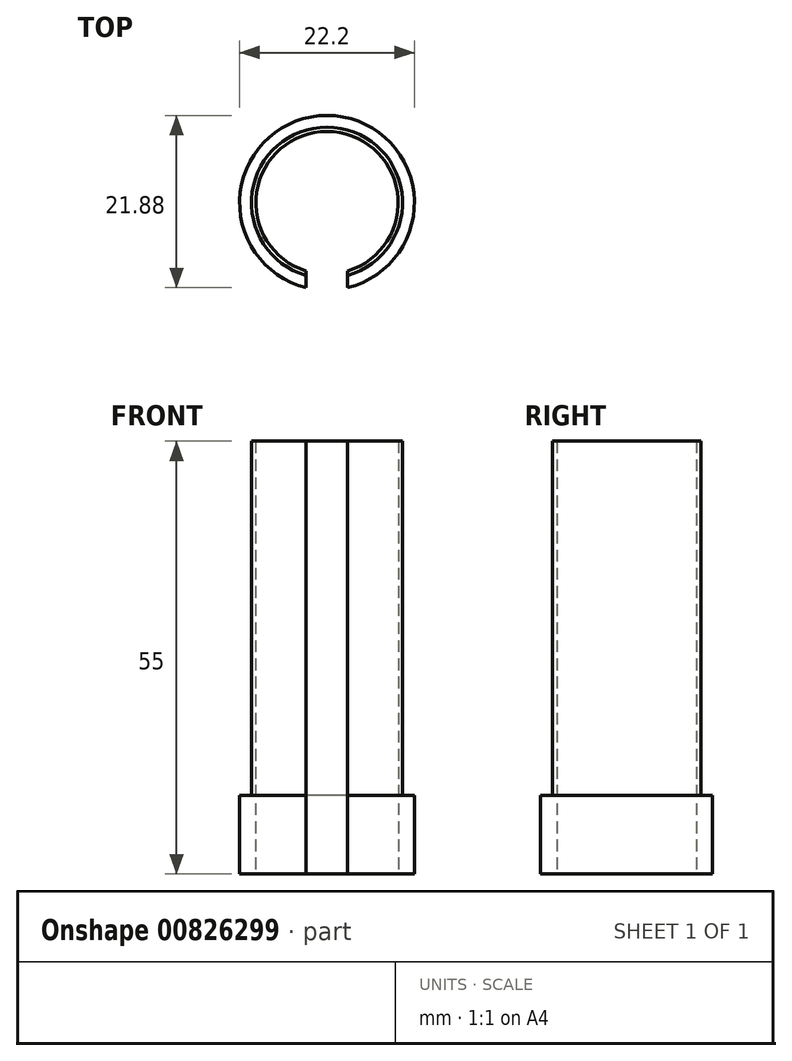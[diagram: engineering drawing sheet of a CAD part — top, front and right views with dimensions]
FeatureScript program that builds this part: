
annotation { "Feature Type Name" : "Feature", "Feature Type Description" : "" }
export const myFeature = defineFeature(function(context is Context, id is Id, definition is map)
    precondition{}
    {
        {
            var Q0;
            Q0=qCreatedBy(makeId("Top.planeOp"),FACE);
            var sketch = newSketch(context, id + "F0", { "sketchPlane" : qUnion([Q0])});
            skArc(sketch, "E0", {"start": v(2.64, -8.66) * mm, "mid": v(0, 9.05) * mm, "end": v(-2.64, -8.66) * mm});
            skArc(sketch, "E1", {"start": v(2.64, -9.23) * mm, "mid": v(0, 9.6) * mm, "end": v(-2.64, -9.23) * mm});
            skArc(sketch, "E2", {"start": v(2.64, -10.78) * mm, "mid": v(0, 11.1) * mm, "end": v(-2.64, -10.78) * mm});
            skLineSegment(sketch, "E3", {"start": v(-2.64, -8.66) * mm, "end": v(-2.64, -10.78) * mm});
            skLineSegment(sketch, "E4", {"start": v(2.64, -8.66) * mm, "end": v(2.64, -10.78) * mm});
            skSolve(sketch);
        }
        {
            var Q0;
            {var subQ0=sQuery(id+"F0.wireOp",EDGE,"E0");Q0=makeQuery(id+"F0.imprint","IMPRINT",FACE,{"disambiguationData":[TD([[makeQuery(id+"F0.imprint","IMPRINT",EDGE,{"derivedFrom":subQ0}),-1.0]])]});}
            extrude(context, id + "F1", {"entities" : qUnion([Q0]), "depth" : 55 * mm, "offsetDistance" : 25 * mm});
        }
        {
            var Q0;
            {var subQ0=sQuery(id+"F0.wireOp",EDGE,"E1");Q0=makeQuery(id+"F0.imprint","IMPRINT",FACE,{"disambiguationData":[TD([[makeQuery(id+"F0.imprint","IMPRINT",EDGE,{"derivedFrom":subQ0}),-1.0]])]});}
            extrude(context, id + "F2", {"entities" : qUnion([Q0]), "operationType" : NewBodyOperationType.ADD, "depth" : 10 * mm, "offsetDistance" : 25 * mm});
        }
    });
